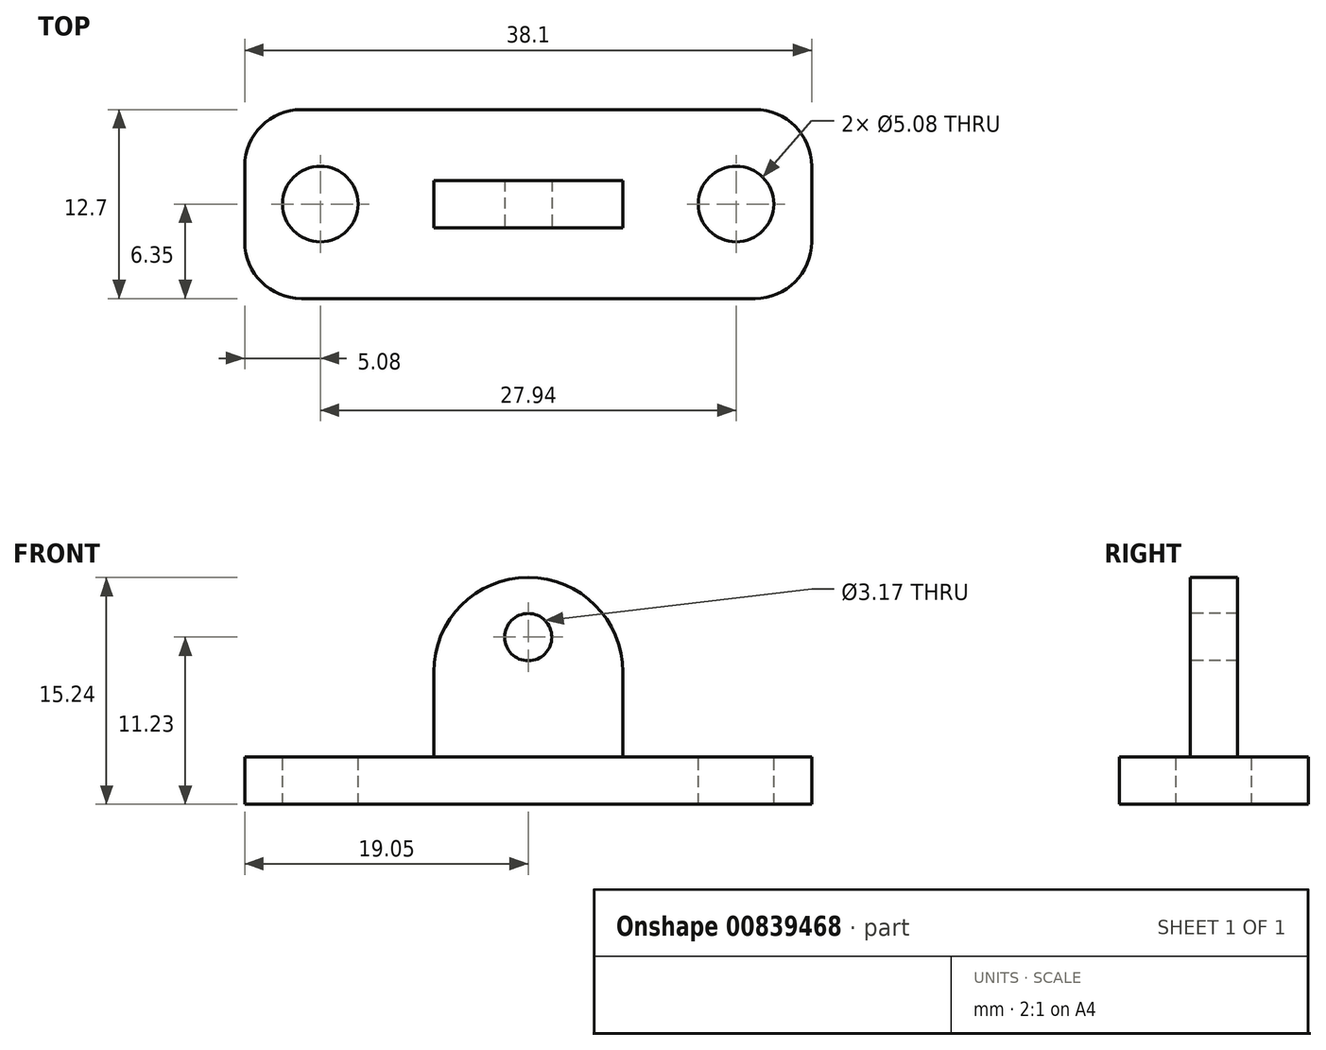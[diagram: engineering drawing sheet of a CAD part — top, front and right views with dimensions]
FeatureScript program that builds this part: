
annotation { "Feature Type Name" : "Feature", "Feature Type Description" : "" }
export const myFeature = defineFeature(function(context is Context, id is Id, definition is map)
    precondition{}
    {
        {
            var Q0;
            Q0=qCreatedBy(makeId("Top.planeOp"),FACE);
            var sketch = newSketch(context, id + "F0", { "sketchPlane" : qUnion([Q0])});
            skLineSegment(sketch, "E0.bottom", {"start": v(19.05, -6.35) * mm, "end": v(-19.05, -6.35) * mm});
            skLineSegment(sketch, "E0.top", {"start": v(19.05, 6.35) * mm, "end": v(-19.05, 6.35) * mm});
            skLineSegment(sketch, "E0.left", {"start": v(19.05, -6.35) * mm, "end": v(19.05, 6.35) * mm});
            skLineSegment(sketch, "E0.right", {"start": v(-19.05, -6.35) * mm, "end": v(-19.05, 6.35) * mm});
            skPoint(sketch, "E0.middle", {"position": v(0, 0) * mm});
            skLineSegment(sketch, "E1.bottom", {"start": v(6.35, -1.59) * mm, "end": v(-6.35, -1.59) * mm});
            skLineSegment(sketch, "E1.top", {"start": v(6.35, 1.59) * mm, "end": v(-6.35, 1.59) * mm});
            skLineSegment(sketch, "E1.left", {"start": v(6.35, -1.59) * mm, "end": v(6.35, 1.59) * mm});
            skLineSegment(sketch, "E1.right", {"start": v(-6.35, -1.59) * mm, "end": v(-6.35, 1.59) * mm});
            skSolve(sketch);
        }
        {
            var Q0;
            Q0=makeQuery(id+"F0.imprint","IMPRINT",FACE,{"disambiguationData":[TD([[makeQuery(id+"F0.imprint","IMPRINT",EDGE,{"derivedFrom":sQuery(id+"F0.wireOp",EDGE,"E0.bottom")}),-1.0]])]});
            extrude(context, id + "F1", {"entities" : qUnion([Q0]), "depth" : 3.17 * mm, "offsetDistance" : 25.4 * mm});
        }
        {
            var Q0;
            Q0=makeQuery(id+"F0.imprint","IMPRINT",FACE,{"disambiguationData":[TD([[makeQuery(id+"F0.imprint","IMPRINT",EDGE,{"derivedFrom":sQuery(id+"F0.wireOp",EDGE,"E1.bottom")}),-1.0]])]});
            extrude(context, id + "F2", {"entities" : qUnion([Q0]), "operationType" : NewBodyOperationType.ADD, "depth" : 15.24 * mm, "offsetDistance" : 25.4 * mm});
        }
        {
            var Q0;
            Q0=makeQuery(id+"F2.opExtrude","CAP_EDGE",EDGE,{"disambiguationData":[OSD([sQuery(id+"F0.wireOp",EDGE,"E1.right")])],"isStart":false});
            var Q1;
            Q1=makeQuery(id+"F2.opExtrude","CAP_EDGE",EDGE,{"disambiguationData":[OSD([sQuery(id+"F0.wireOp",EDGE,"E1.left")])],"isStart":false});
            fillet(context, id + "F3", {"entities" : qUnion([Q0, Q1]), "radius" : 6.35 * mm, "tangentPropagation" : true, "allowEdgeOverflow" : false});
        }
        {
            var Q0;
            Q0=makeQuery(id+"F1.opExtrude","SWEPT_EDGE",EDGE,{"disambiguationData":[OSD([sQuery(id+"F0.wireOp",EDGE,"E0.bottom"),sQuery(id+"F0.wireOp",EDGE,"E0.right")])]});
            var Q1;
            Q1=makeQuery(id+"F1.opExtrude","SWEPT_EDGE",EDGE,{"disambiguationData":[OSD([sQuery(id+"F0.wireOp",EDGE,"E0.top"),sQuery(id+"F0.wireOp",EDGE,"E0.right")])]});
            var Q2;
            Q2=makeQuery(id+"F1.opExtrude","SWEPT_EDGE",EDGE,{"disambiguationData":[OSD([sQuery(id+"F0.wireOp",EDGE,"E0.top"),sQuery(id+"F0.wireOp",EDGE,"E0.left")])]});
            var Q3;
            Q3=makeQuery(id+"F1.opExtrude","SWEPT_EDGE",EDGE,{"disambiguationData":[OSD([sQuery(id+"F0.wireOp",EDGE,"E0.bottom"),sQuery(id+"F0.wireOp",EDGE,"E0.left")])]});
            var Q4;
            Q4=makeQuery(id+"F1.opExtrude","CAP_EDGE",EDGE,{"disambiguationData":[OSD([sQuery(id+"F0.wireOp",EDGE,"E1.bottom")])],"isStart":false});
            var Q5;
            Q5=makeQuery(id+"F1.opExtrude","CAP_EDGE",EDGE,{"disambiguationData":[OSD([sQuery(id+"F0.wireOp",EDGE,"E1.top")])],"isStart":false});
            var Q6;
            Q6=makeQuery(id+"F1.opExtrude","CAP_EDGE",EDGE,{"disambiguationData":[OSD([sQuery(id+"F0.wireOp",EDGE,"E1.left")])],"isStart":false});
            var Q7;
            Q7=makeQuery(id+"F1.opExtrude","CAP_EDGE",EDGE,{"disambiguationData":[OSD([sQuery(id+"F0.wireOp",EDGE,"E1.right")])],"isStart":false});
            fillet(context, id + "F4", {"entities" : qUnion([Q0, Q1, Q2, Q3, Q4, Q5, Q6, Q7]), "radius" : 3.8 * mm, "tangentPropagation" : true, "allowEdgeOverflow" : false});
        }
        {
            var Q0;
            Q0=makeQuery(id+"F1.opExtrude","SWEPT_FACE",FACE,{"disambiguationData":[OSD([sQuery(id+"F0.wireOp",EDGE,"E0.bottom")])]});
            var sketch = newSketch(context, id + "F5", { "sketchPlane" : qUnion([Q0])});
            skCircle(sketch, "E2", {"center": v(0, 11.23) * mm, "radius": 1.59 * mm});
            skSolve(sketch);
        }
        {
            var Q0;
            Q0 = qSketchRegion(id + "F5", true);
            extrude(context, id + "F6", {"entities" : qUnion([Q0]), "operationType" : NewBodyOperationType.REMOVE, "endBound" : BoundingType.THROUGH_ALL, "oppositeDirection" : true, "depth" : 25.4 * mm, "offsetDistance" : 25.4 * mm});
        }
        {
            var Q0;
            Q0=makeQuery(id+"F1.opExtrude","CAP_FACE",FACE,{"disambiguationData":[OSD([sQuery(id+"F0.wireOp",EDGE,"E0.bottom"),sQuery(id+"F0.wireOp",EDGE,"E0.top"),sQuery(id+"F0.wireOp",EDGE,"E0.left"),sQuery(id+"F0.wireOp",EDGE,"E0.right"),sQuery(id+"F0.wireOp",EDGE,"E1.bottom"),sQuery(id+"F0.wireOp",EDGE,"E1.top"),sQuery(id+"F0.wireOp",EDGE,"E1.left"),sQuery(id+"F0.wireOp",EDGE,"E1.right")])],"isStart":false});
            var sketch = newSketch(context, id + "F7", { "sketchPlane" : qUnion([Q0])});
            skCircle(sketch, "E3", {"center": v(-13.97, 0) * mm, "radius": 2.54 * mm});
            skCircle(sketch, "E4", {"center": v(13.97, 0) * mm, "radius": 2.54 * mm});
            skSolve(sketch);
        }
        {
            var Q0;
            Q0 = qSketchRegion(id + "F7", true);
            extrude(context, id + "F8", {"entities" : qUnion([Q0]), "operationType" : NewBodyOperationType.REMOVE, "endBound" : BoundingType.THROUGH_ALL, "oppositeDirection" : true, "depth" : 25.4 * mm, "offsetDistance" : 25.4 * mm});
        }
    });
